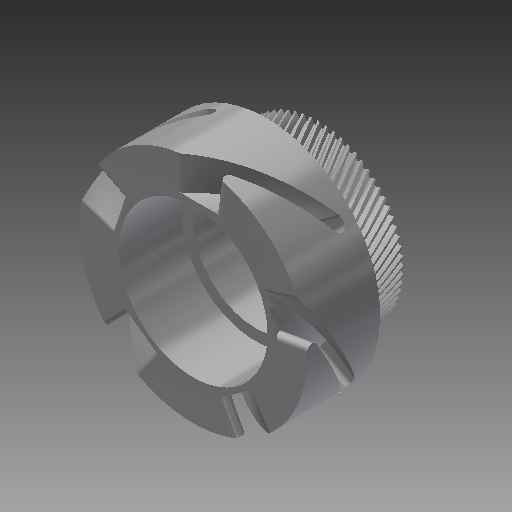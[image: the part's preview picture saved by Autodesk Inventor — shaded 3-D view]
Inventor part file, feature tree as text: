
AUTODESK INVENTOR PART (.ipt)
format: ipt  version: 2018 (Build 220112000, 112)  size: 1,522,688 bytes
history: native  units: mm (DEFAULTED — no unit token found)
features: sketch x7, extrude x5, plane x3, other x3, fillet x2, projected_geometry x2, helix x1, pattern_circular x1
ambient origin geometry x8: Origin, YZ Plane, XZ Plane, XY Plane, X Axis, Y Axis, Z Axis, Center Point
bodies: Solid1 (feature_tree)
feature tree (24):
  extrude  "Extrusion1"  Depth=12.7mm TaperAngle=0.0deg
  plane  "Work Plane1"
  plane  "Work Plane2"
  plane  "Work Plane3"
  other  "Spur Gear"
  extrude  "Extrusion2"  Depth=76.2mm TaperAngle=0.0deg
  extrude  "Extrusion3"  TaperAngle=0.0deg  [1 undecoded]
  extrude  "Extrusion4"  Depth=31.75mm
  helix  "Coil1"  [1 undecoded]
  fillet  "Fillet1"  [1 undecoded]
  fillet  "Fillet2"  [1 undecoded]
  pattern_circular  "Circular Pattern1"  [2 undecoded]
  extrude  "Extrusion5"  Depth=38.354mm
  sketch  "Sketch1"  dims[d0=51.854614mm d1=12.7mm d2=0.0mm]
  sketch  "Sketch2"  dims[d3=50.947674mm d4=76.2mm d5=0.0mm]
  other  "Srf1"
  sketch  "Sketch3"  dims[d6=0.0mm d7=0.455303mm d9=0.0mm]
  sketch  "Sketch4"  dims[d14=0.0mm d15=31.75mm d16=0.0mm d17=0.0mm d18=0.0mm]
  sketch  "Sketch5"  dims[d19=31.75mm]
  projected_geometry  "Projected Loop1"
  sketch  "Sketch6"  dims[d20=69.342mm]
  projected_geometry  "Projected Loop2"
  sketch  "Sketch7"  dims[d21=45.212mm d22=25.4mm d23=0.0mm d24=38.354mm d25=50.8mm d26=0.0mm d27=6.35mm d28=0.0mm d29=3.81mm d30=3.81mm d31=127.0mm d32=19.05mm d33=5.0mm d34=0.0mm d35=90.0deg d36=90.0deg d37=0.0mm d38=0.0mm d39=1.5875mm d40=1.5875mm d41=50.0mm d42=360.0deg d44=24.13mm d45=25.4mm d46=8.255mm d47=3.175mm d48=0.0mm]
  other  "Pitch Diameter"
note: 6 required parameter values undecoded (feature->parameter linkage not recoverable at this tier; creation-order binding heuristic only, values carry confidence <= 0.55)
